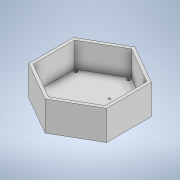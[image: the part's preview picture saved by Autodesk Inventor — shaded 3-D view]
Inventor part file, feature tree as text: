
AUTODESK INVENTOR PART (.ipt)
format: ipt  version: 2020 (Build 240168000, 168)  size: 230,400 bytes
history: native  units: mm
features: extrude x5, sketch x3
ambient origin geometry x8: Origin, YZ Plane, XZ Plane, XY Plane, X Axis, Y Axis, Z Axis, Center Point
bodies: Solid1 (feature_tree)
feature tree (8):
  sketch  "Sketch1"  dims[d1=70.0mm d2=70.0mm]
  extrude  "Extrusion1"  Depth=70.0mm
  extrude  "Extrusion2"  Depth=70.0mm
  extrude  "Extrusion3"  TaperAngle=120.0deg  [1 undecoded]
  sketch  "Sketch3"  dims[d5=70.0mm d6=120.0deg d7=120.0deg d9=120.0deg d10=120.0deg d11=120.0deg d15=5.0mm d16=131.243557mm d18=0.0mm d20=0.0mm d22=3.81mm d23=41.91mm d24=4.45mm d25=44.485mm d26=3.81mm d27=3.81mm d28=41.91mm d29=44.485mm d30=1.0mm d31=14.045mm d32=5.0mm d33=0.0mm d35=5.0mm d36=150.0deg d37=5.0mm d38=90.0deg d39=5.0mm d40=30.0deg d42=5.0mm d43=5.0mm d44=5.0mm d45=60.0deg d47=5.0mm d48=5.0mm d49=60.0deg d50=5.0mm d51=5.0mm d52=5.0mm d53=2.5mm d54=2.5mm d55=2.5mm d56=2.5mm d57=2.5mm d58=2.5mm d59=3.75mm d60=0.0mm d61=7.5mm d62=0.0mm]
  extrude  "Extrusion4"  TaperAngle=120.0deg  [1 undecoded]
  extrude  "Extrusion5"  TaperAngle=120.0deg  [1 undecoded]
  sketch  "Sketch2"  dims[d3=70.0mm d4=70.0mm]
note: 3 required parameter values undecoded (feature->parameter linkage not recoverable at this tier; creation-order binding heuristic only, values carry confidence <= 0.55)
